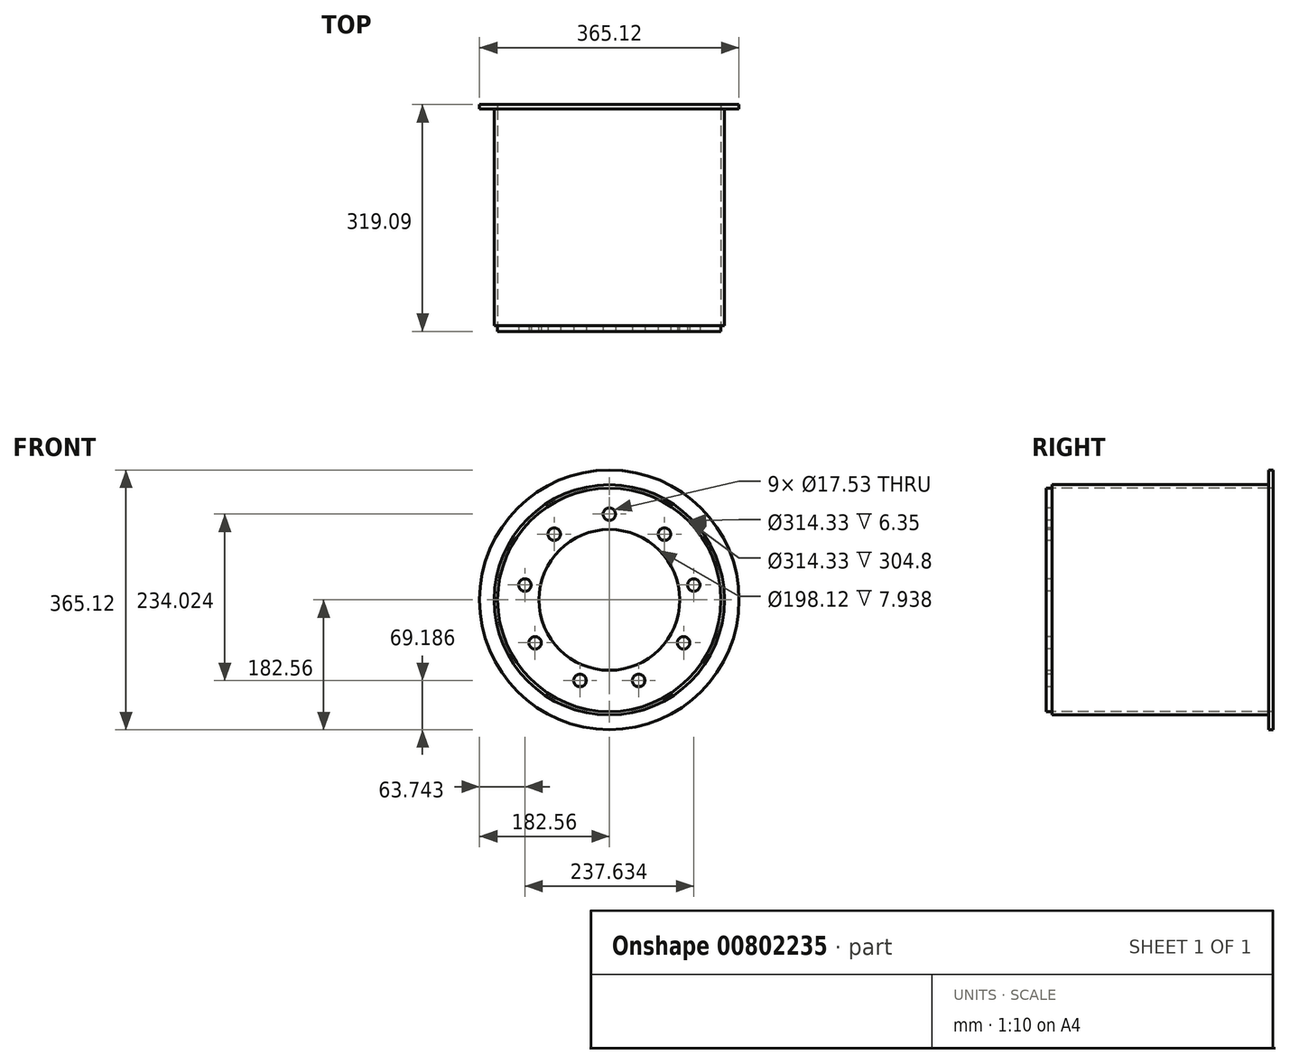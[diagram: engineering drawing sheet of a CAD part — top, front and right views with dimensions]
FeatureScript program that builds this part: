
annotation { "Feature Type Name" : "Feature", "Feature Type Description" : "" }
export const myFeature = defineFeature(function(context is Context, id is Id, definition is map)
    precondition{}
    {
        {
            var Q0;
            Q0=qCreatedBy(makeId("Front.planeOp"),FACE);
            var sketch = newSketch(context, id + "F0", { "sketchPlane" : qUnion([Q0])});
            skCircle(sketch, "E0", {"center": v(0, 0) * mm, "radius": 99.06 * mm});
            skCircle(sketch, "E1", {"center": v(0, 0) * mm, "radius": 157.16 * mm});
            skSolve(sketch);
        }
        {
            var Q0;
            Q0 = qSketchRegion(id + "F0", true);
            extrude(context, id + "F1", {"entities" : qUnion([Q0]), "depth" : 7.94 * mm, "offsetDistance" : 25.4 * mm});
        }
        {
            var Q0;
            Q0=makeQuery(id+"F1.opExtrude","CAP_FACE",FACE,{"disambiguationData":[OSD([sQuery(id+"F0.wireOp",EDGE,"E0"),sQuery(id+"F0.wireOp",EDGE,"E1")])],"isStart":false});
            var sketch = newSketch(context, id + "F2", { "sketchPlane" : qUnion([Q0])});
            skCircle(sketch, "E2", {"center": v(0, 0) * mm, "radius": 120.65 * mm, "construction": true});
            skCircle(sketch, "E3", {"center": v(0, 120.65) * mm, "radius": 8.76 * mm});
            skCircle(sketch, "E4.1.0", {"center": v(-77.55, 92.42) * mm, "radius": 8.76 * mm});
            skCircle(sketch, "E4.2.0", {"center": v(-118.82, 20.95) * mm, "radius": 8.76 * mm});
            skCircle(sketch, "E4.3.0", {"center": v(-104.49, -60.32) * mm, "radius": 8.76 * mm});
            skCircle(sketch, "E4.4.0", {"center": v(-41.26, -113.37) * mm, "radius": 8.76 * mm});
            skCircle(sketch, "E4.5.0", {"center": v(41.26, -113.37) * mm, "radius": 8.76 * mm});
            skCircle(sketch, "E4.6.0", {"center": v(104.49, -60.33) * mm, "radius": 8.76 * mm});
            skCircle(sketch, "E4.7.0", {"center": v(118.82, 20.95) * mm, "radius": 8.76 * mm});
            skCircle(sketch, "E4.8.0", {"center": v(77.55, 92.42) * mm, "radius": 8.76 * mm});
            skSolve(sketch);
        }
        {
            var Q0;
            Q0 = qSketchRegion(id + "F2", true);
            extrude(context, id + "F3", {"entities" : qUnion([Q0]), "operationType" : NewBodyOperationType.REMOVE, "endBound" : BoundingType.THROUGH_ALL, "oppositeDirection" : true, "depth" : 25.4 * mm, "offsetDistance" : 25.4 * mm});
        }
        {
            var Q0;
            Q0=makeQuery(id+"F1.opExtrude","CAP_FACE",FACE,{"disambiguationData":[OSD([sQuery(id+"F0.wireOp",EDGE,"E0"),sQuery(id+"F0.wireOp",EDGE,"E1")])],"isStart":true});
            var sketch = newSketch(context, id + "F4", { "sketchPlane" : qUnion([Q0])});
            skCircle(sketch, "E5", {"center": v(0, 0) * mm, "radius": 157.16 * mm});
            skCircle(sketch, "E6", {"center": v(0, 0) * mm, "radius": 161.93 * mm});
            skPoint(sketch, "E7", {"position": v(0, 157.16) * mm});
            skPoint(sketch, "E8", {"position": v(0, 161.93) * mm});
            skSolve(sketch);
        }
        {
            var Q0;
            Q0 = qSketchRegion(id + "F4", true);
            extrude(context, id + "F5", {"entities" : qUnion([Q0]), "depth" : 304.8 * mm, "offsetDistance" : 25.4 * mm});
        }
        {
            var Q0;
            Q0=makeQuery(id+"F5.opExtrude","CAP_FACE",FACE,{"disambiguationData":[OSD([sQuery(id+"F4.wireOp",EDGE,"E5"),sQuery(id+"F4.wireOp",EDGE,"E6")])],"isStart":false});
            var sketch = newSketch(context, id + "F6", { "sketchPlane" : qUnion([Q0])});
            skCircle(sketch, "E9", {"center": v(0, 0) * mm, "radius": 157.16 * mm});
            skCircle(sketch, "E10", {"center": v(0, 0) * mm, "radius": 182.56 * mm});
            skPoint(sketch, "E11", {"position": v(0, 157.16) * mm});
            skPoint(sketch, "E12", {"position": v(0, 182.56) * mm});
            skSolve(sketch);
        }
        {
            var Q0;
            Q0 = qSketchRegion(id + "F6", true);
            extrude(context, id + "F7", {"entities" : qUnion([Q0]), "depth" : 6.35 * mm, "offsetDistance" : 25.4 * mm});
        }
    });
